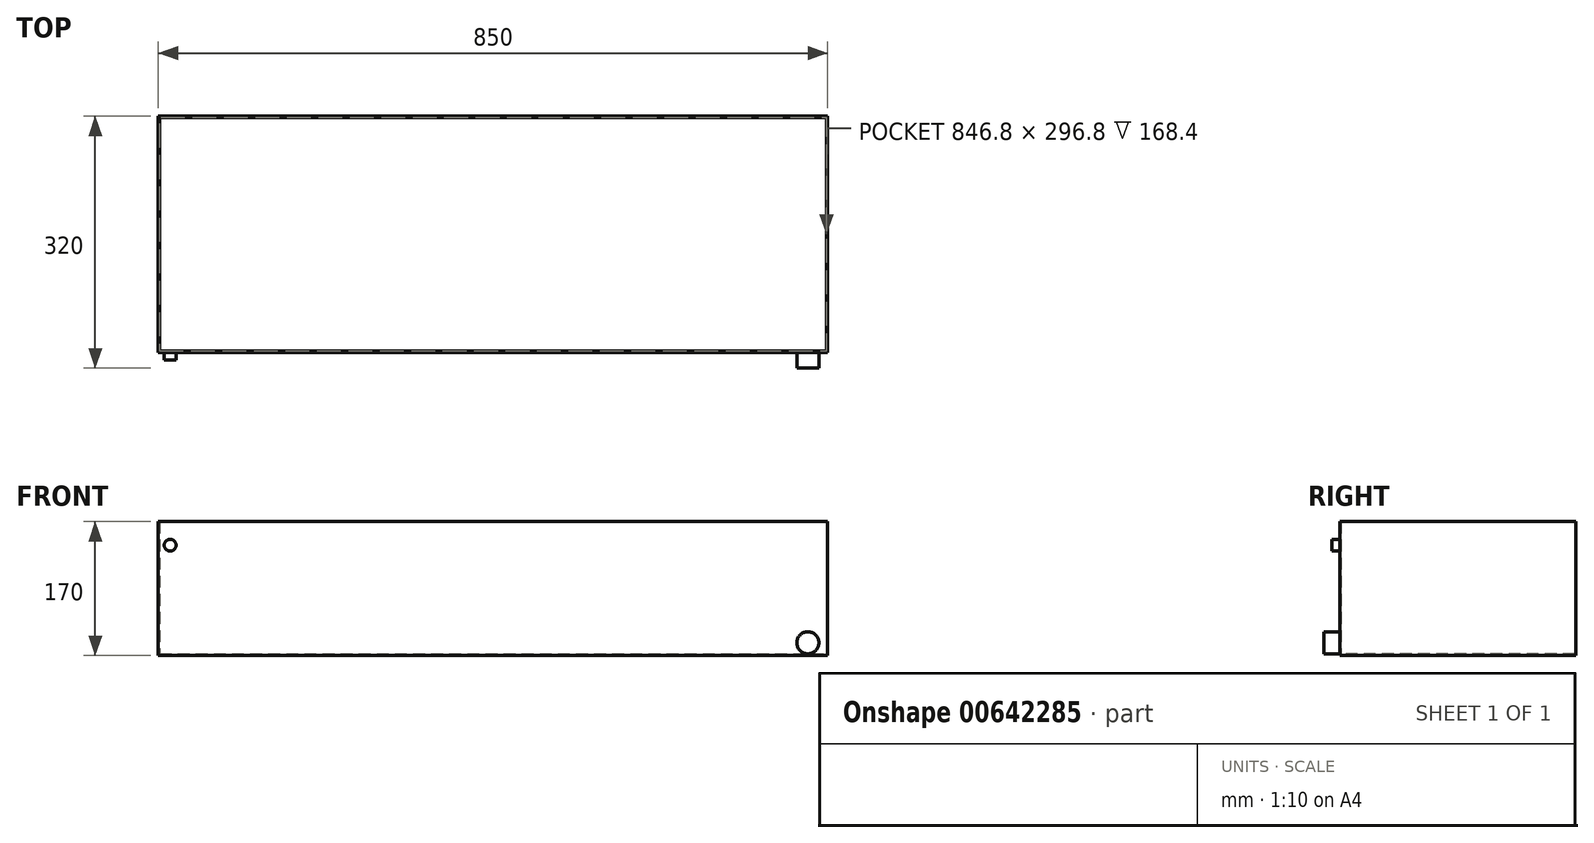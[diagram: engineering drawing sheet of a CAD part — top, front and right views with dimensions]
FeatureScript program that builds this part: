
annotation { "Feature Type Name" : "Feature", "Feature Type Description" : "" }
export const myFeature = defineFeature(function(context is Context, id is Id, definition is map)
    precondition{}
    {
        {
            var Q0;
            Q0=qCreatedBy(makeId("Top.planeOp"),FACE);
            var sketch = newSketch(context, id + "F0", { "sketchPlane" : qUnion([Q0])});
            skLineSegment(sketch, "E0.bottom", {"start": v(-425, 150) * mm, "end": v(425, 150) * mm});
            skLineSegment(sketch, "E0.top", {"start": v(-425, -150) * mm, "end": v(425, -150) * mm});
            skLineSegment(sketch, "E0.left", {"start": v(-425, 150) * mm, "end": v(-425, -150) * mm});
            skLineSegment(sketch, "E0.right", {"start": v(425, 150) * mm, "end": v(425, -150) * mm});
            skSolve(sketch);
        }
        {
            var Q0;
            Q0 = qSketchRegion(id + "F0", true);
            extrude(context, id + "F1", {"entities" : qUnion([Q0]), "depth" : 85 * mm, "offsetDistance" : 25 * mm, "hasSecondDirection" : true, "secondDirectionOppositeDirection" : true, "secondDirectionDepth" : 85 * mm});
        }
        {
            var Q0;
            Q0=makeQuery(id+"F1.opExtrude","CAP_FACE",FACE,{"disambiguationData":[OSD([sQuery(id+"F0.wireOp",EDGE,"E0.bottom"),sQuery(id+"F0.wireOp",EDGE,"E0.top"),sQuery(id+"F0.wireOp",EDGE,"E0.left"),sQuery(id+"F0.wireOp",EDGE,"E0.right")])],"isStart":false});
            shell(context, id + "F2", {"entities" : qUnion([Q0]), "thickness" : 1.6 * mm});
        }
        {
            var Q0;
            Q0=makeQuery(id+"F1.opExtrude","SWEPT_FACE",FACE,{"disambiguationData":[OSD([sQuery(id+"F0.wireOp",EDGE,"E0.top")])]});
            var sketch = newSketch(context, id + "F3", { "sketchPlane" : qUnion([Q0])});
            skCircle(sketch, "E1", {"center": v(400, -69) * mm, "radius": 14 * mm});
            skSolve(sketch);
        }
        {
            var Q0;
            Q0=makeQuery(id+"F3.imprint","IMPRINT",FACE,{"disambiguationData":[TD([[makeQuery(id+"F3.imprint","IMPRINT",EDGE,{"derivedFrom":sQuery(id+"F3.wireOp",EDGE,"E1")}),1.0]])]});
            extrude(context, id + "F4", {"entities" : qUnion([Q0]), "operationType" : NewBodyOperationType.ADD, "depth" : 20 * mm, "offsetDistance" : 25 * mm});
        }
        {
            var Q0;
            Q0=makeQuery(id+"F1.opExtrude","SWEPT_FACE",FACE,{"disambiguationData":[OSD([sQuery(id+"F0.wireOp",EDGE,"E0.top")])]});
            var sketch = newSketch(context, id + "F5", { "sketchPlane" : qUnion([Q0])});
            skCircle(sketch, "E2", {"center": v(-410, 55) * mm, "radius": 7.5 * mm});
            skSolve(sketch);
        }
        {
            var Q0;
            Q0 = qSketchRegion(id + "F5", true);
            extrude(context, id + "F6", {"entities" : qUnion([Q0]), "operationType" : NewBodyOperationType.ADD, "depth" : 10 * mm, "offsetDistance" : 25 * mm});
        }
    });
